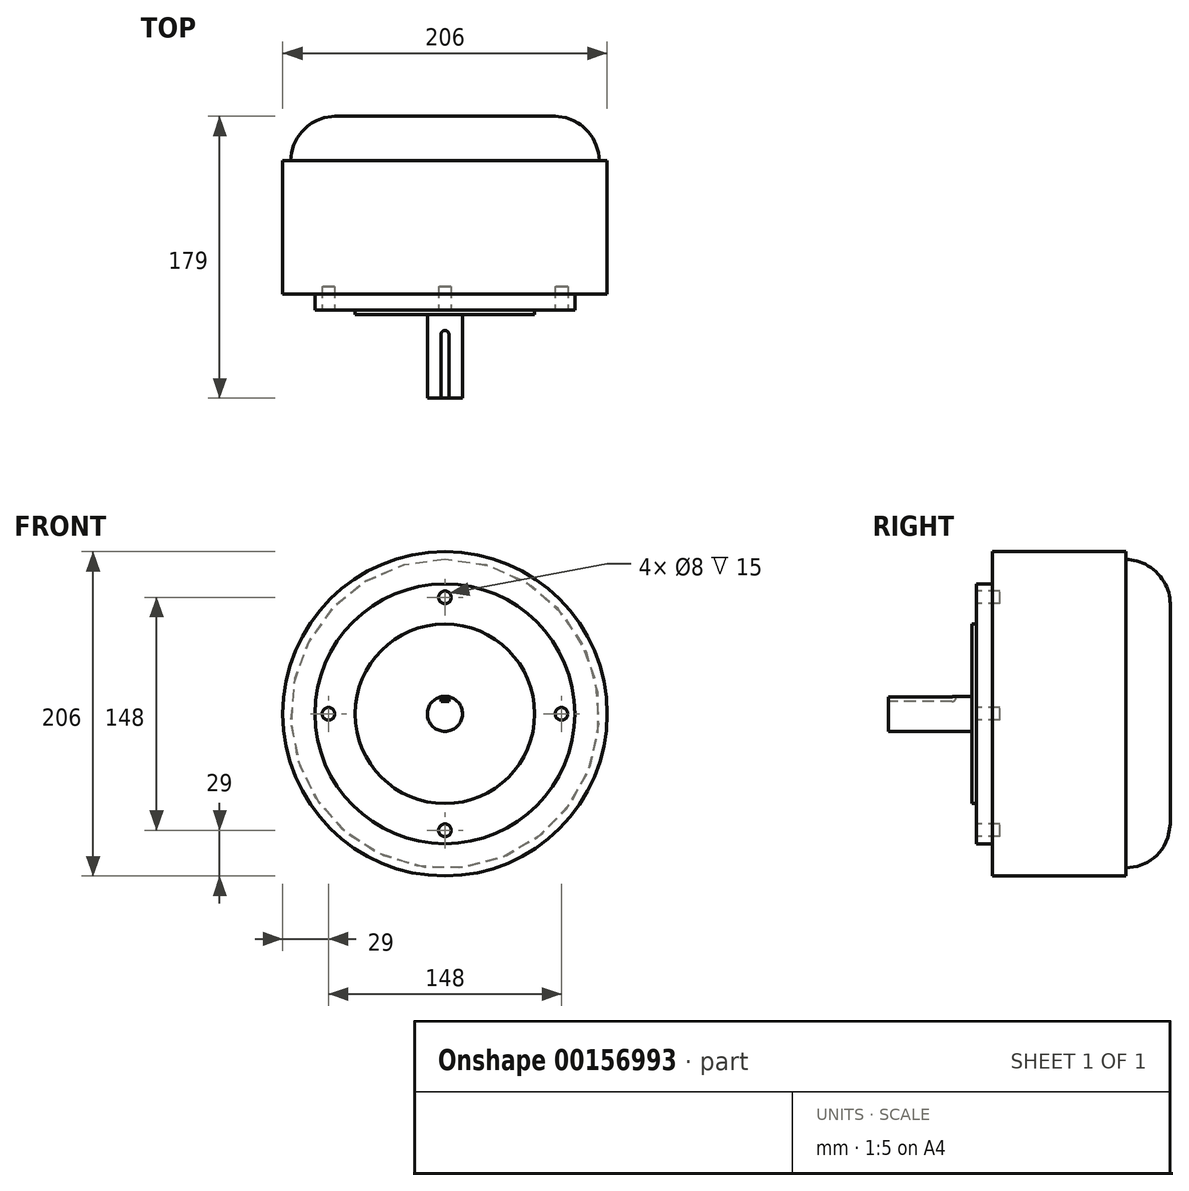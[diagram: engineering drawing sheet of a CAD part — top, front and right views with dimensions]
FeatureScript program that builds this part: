
annotation { "Feature Type Name" : "Feature", "Feature Type Description" : "" }
export const myFeature = defineFeature(function(context is Context, id is Id, definition is map)
    precondition{}
    {
        {
            var Q0;
            Q0=qCreatedBy(makeId("Front.planeOp"),FACE);
            var sketch = newSketch(context, id + "F0", { "sketchPlane" : qUnion([Q0])});
            skCircle(sketch, "E0", {"center": v(0, 0) * mm, "radius": 103 * mm});
            skSolve(sketch);
        }
        {
            var Q0;
            Q0=makeQuery(id+"F0.imprint","IMPRINT",FACE,{"disambiguationData":[TD([[makeQuery(id+"F0.imprint","IMPRINT",EDGE,{"derivedFrom":sQuery(id+"F0.wireOp",EDGE,"E0")}),1.0]])]});
            extrude(context, id + "F1", {"entities" : qUnion([Q0]), "oppositeDirection" : true, "depth" : 85 * mm});
        }
        {
            var Q0;
            Q0=makeQuery(id+"F1.opExtrude","CAP_FACE",FACE,{"disambiguationData":[OSD([sQuery(id+"F0.wireOp",EDGE,"E0")])],"isStart":true});
            var sketch = newSketch(context, id + "F2", { "sketchPlane" : qUnion([Q0])});
            skCircle(sketch, "E1", {"center": v(0, 0) * mm, "radius": 82.5 * mm});
            skSolve(sketch);
        }
        {
            var Q0;
            Q0=makeQuery(id+"F2.imprint","IMPRINT",FACE,{"disambiguationData":[TD([[makeQuery(id+"F2.imprint","IMPRINT",EDGE,{"derivedFrom":sQuery(id+"F2.wireOp",EDGE,"E1")}),1.0]])]});
            extrude(context, id + "F3", {"entities" : qUnion([Q0]), "operationType" : NewBodyOperationType.ADD, "depth" : 10 * mm});
        }
        {
            var Q0;
            Q0=makeQuery(id+"F3.opExtrude","CAP_FACE",FACE,{"disambiguationData":[OSD([sQuery(id+"F2.wireOp",EDGE,"E1")])],"isStart":false});
            var sketch = newSketch(context, id + "F4", { "sketchPlane" : qUnion([Q0])});
            skCircle(sketch, "E2", {"center": v(0, 0) * mm, "radius": 57 * mm});
            skSolve(sketch);
        }
        {
            var Q0;
            Q0=makeQuery(id+"F4.imprint","IMPRINT",FACE,{"disambiguationData":[TD([[makeQuery(id+"F4.imprint","IMPRINT",EDGE,{"derivedFrom":sQuery(id+"F4.wireOp",EDGE,"E2")}),1.0]])]});
            extrude(context, id + "F5", {"entities" : qUnion([Q0]), "operationType" : NewBodyOperationType.ADD, "depth" : 3 * mm});
        }
        {
            var Q0;
            Q0=makeQuery(id+"F3.opExtrude","CAP_FACE",FACE,{"disambiguationData":[OSD([sQuery(id+"F2.wireOp",EDGE,"E1")])],"isStart":false});
            var sketch = newSketch(context, id + "F6", { "sketchPlane" : qUnion([Q0])});
            skCircle(sketch, "E3", {"center": v(0, 74) * mm, "radius": 4 * mm});
            skCircle(sketch, "E4", {"center": v(0, 0) * mm, "radius": 74 * mm, "construction": true});
            skCircle(sketch, "E5", {"center": v(74, 0) * mm, "radius": 4 * mm});
            skCircle(sketch, "E6", {"center": v(0, -74) * mm, "radius": 4 * mm});
            skCircle(sketch, "E7", {"center": v(-74, 0) * mm, "radius": 4 * mm});
            skSolve(sketch);
        }
        {
            var Q0;
            Q0 = qSketchRegion(id + "F6", true);
            extrude(context, id + "F7", {"entities" : qUnion([Q0]), "operationType" : NewBodyOperationType.REMOVE, "oppositeDirection" : true, "depth" : 15 * mm});
        }
        {
            var Q0;
            Q0=makeQuery(id+"F1.opExtrude","CAP_FACE",FACE,{"disambiguationData":[OSD([sQuery(id+"F0.wireOp",EDGE,"E0")])],"isStart":false});
            var sketch = newSketch(context, id + "F8", { "sketchPlane" : qUnion([Q0])});
            skCircle(sketch, "E8", {"center": v(0, 0) * mm, "radius": 98.03 * mm});
            skSolve(sketch);
        }
        {
            var Q0;
            Q0=makeQuery(id+"F8.imprint","IMPRINT",FACE,{"disambiguationData":[TD([[makeQuery(id+"F8.imprint","IMPRINT",EDGE,{"derivedFrom":sQuery(id+"F8.wireOp",EDGE,"E8")}),1.0]])]});
            extrude(context, id + "F9", {"entities" : qUnion([Q0]), "operationType" : NewBodyOperationType.ADD, "depth" : 28 * mm});
        }
        {
            var Q0;
            Q0=makeQuery(id+"F9.opExtrude","CAP_EDGE",EDGE,{"disambiguationData":[OSD([sQuery(id+"F8.wireOp",EDGE,"E8")])],"isStart":false});
            fillet(context, id + "F10", {"entities" : qUnion([Q0]), "radius" : 28 * mm, "tangentPropagation" : true, "rho" : .4, "crossSection" : FilletCrossSection.CONIC, "allowEdgeOverflow" : false});
        }
        {
            var Q0;
            Q0=makeQuery(id+"F5.opExtrude","CAP_FACE",FACE,{"disambiguationData":[OSD([sQuery(id+"F4.wireOp",EDGE,"E2")])],"isStart":false});
            var sketch = newSketch(context, id + "F11", { "sketchPlane" : qUnion([Q0])});
            skCircle(sketch, "E9", {"center": v(0, 0) * mm, "radius": 11.15 * mm});
            skSolve(sketch);
        }
        {
            var Q0;
            Q0 = qSketchRegion(id + "F11", true);
            extrude(context, id + "F12", {"entities" : qUnion([Q0]), "depth" : 53 * mm});
        }
        {
            var Q0;
            Q0=makeQuery(id+"F12.opExtrude","CAP_FACE",FACE,{"disambiguationData":[OSD([sQuery(id+"F11.wireOp",EDGE,"E9")])],"isStart":false});
            var sketch = newSketch(context, id + "F13", { "sketchPlane" : qUnion([Q0])});
            skLineSegment(sketch, "E10.top", {"start": v(-2.5, 7.85) * mm, "end": v(2.5, 7.85) * mm});
            skLineSegment(sketch, "E10.left", {"start": v(-2.5, 10.87) * mm, "end": v(-2.5, 7.85) * mm});
            skLineSegment(sketch, "E10.right", {"start": v(2.5, 10.87) * mm, "end": v(2.5, 7.85) * mm});
            skPoint(sketch, "E11", {"position": v(0, 7.85) * mm});
            skArc(sketch, "E12.0", {"start": v(2.5, 10.87) * mm, "mid": v(0, 11.15) * mm, "end": v(-2.5, 10.87) * mm});
            skSolve(sketch);
        }
        {
            var Q0;
            Q0=makeQuery(id+"F13.imprint","IMPRINT",FACE,{"disambiguationData":[TD([[makeQuery(id+"F13.imprint","IMPRINT",EDGE,{"derivedFrom":sQuery(id+"F13.wireOp",EDGE,"E10.top")}),1.0]])]});
            var Q1;
            Q1 = qSketchRegion(id + "F13", true);
            extrude(context, id + "F14", {"entities" : qUnion([Q0, Q1]), "operationType" : NewBodyOperationType.REMOVE, "oppositeDirection" : true, "depth" : 43 * mm});
        }
        {
            var Q0;
            Q0=makeQuery(id+"F14.boolean.opBoolean","COPY",EDGE,{"derivedFrom":makeQuery(id+"F14.opExtrude","CAP_EDGE",EDGE,{"disambiguationData":[OSD([sQuery(id+"F13.wireOp",EDGE,"E10.right")])],"isStart":false})});
            var Q1;
            Q1=makeQuery(id+"F14.boolean.opBoolean","COPY",EDGE,{"derivedFrom":makeQuery(id+"F14.opExtrude","CAP_EDGE",EDGE,{"disambiguationData":[OSD([sQuery(id+"F13.wireOp",EDGE,"E10.left")])],"isStart":false})});
            var Q2;
            Q2=makeQuery(id+"F14.boolean.opBoolean","COPY",EDGE,{"derivedFrom":makeQuery(id+"F14.opExtrude","CAP_EDGE",EDGE,{"disambiguationData":[OSD([sQuery(id+"F13.wireOp",EDGE,"E10.top")])],"isStart":false})});
            fillet(context, id + "F15", {"entities" : qUnion([Q0, Q1, Q2]), "radius" : 2.5 * mm, "tangentPropagation" : true, "allowEdgeOverflow" : false});
        }
    });
